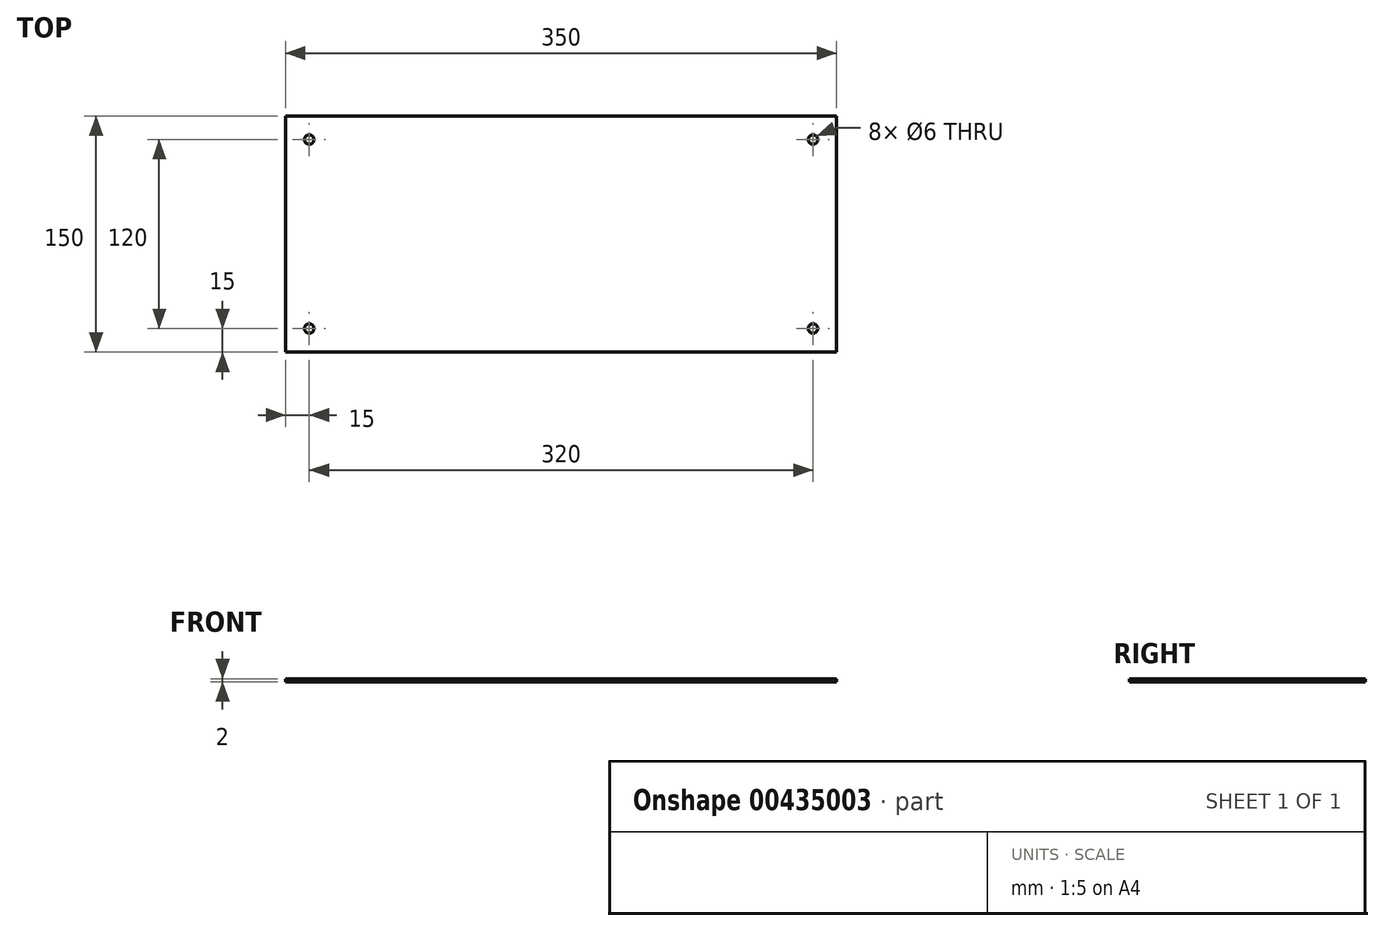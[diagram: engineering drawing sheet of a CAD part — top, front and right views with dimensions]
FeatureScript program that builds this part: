
annotation { "Feature Type Name" : "Feature", "Feature Type Description" : "" }
export const myFeature = defineFeature(function(context is Context, id is Id, definition is map)
    precondition{}
    {
        {
            var Q0;
            Q0=qCreatedBy(makeId("Top.planeOp"),FACE);
            var sketch = newSketch(context, id + "F0", { "sketchPlane" : qUnion([Q0])});
            skLineSegment(sketch, "E0.bottom", {"start": v(-175, -75) * mm, "end": v(175, -75) * mm});
            skLineSegment(sketch, "E0.top", {"start": v(-175, 75) * mm, "end": v(175, 75) * mm});
            skLineSegment(sketch, "E0.left", {"start": v(-175, -75) * mm, "end": v(-175, 75) * mm});
            skLineSegment(sketch, "E0.right", {"start": v(175, -75) * mm, "end": v(175, 75) * mm});
            skPoint(sketch, "E0.middle", {"position": v(0, 0) * mm});
            skSolve(sketch);
        }
        {
            var Q0;
            Q0 = qSketchRegion(id + "F0", true);
            extrude(context, id + "F1", {"entities" : qUnion([Q0]), "depth" : 2 * mm});
        }
        {
            var Q0;
            Q0=makeQuery(id+"F1.opExtrude","CAP_FACE",FACE,{"disambiguationData":[OSD([sQuery(id+"F0.wireOp",EDGE,"E0.bottom"),sQuery(id+"F0.wireOp",EDGE,"E0.top"),sQuery(id+"F0.wireOp",EDGE,"E0.left"),sQuery(id+"F0.wireOp",EDGE,"E0.right")])],"isStart":false});
            var sketch = newSketch(context, id + "F2", { "sketchPlane" : qUnion([Q0])});
            skLineSegment(sketch, "E1", {"start": v(-175, 75) * mm, "end": v(-175, 60) * mm});
            skLineSegment(sketch, "E2", {"start": v(-175, 60) * mm, "end": v(-160, 60) * mm});
            skLineSegment(sketch, "E3", {"start": v(-160, 60) * mm, "end": v(-160, -60) * mm});
            skLineSegment(sketch, "E4", {"start": v(-160, -60) * mm, "end": v(160, -60) * mm});
            skLineSegment(sketch, "E5", {"start": v(160, -60) * mm, "end": v(160, 60) * mm});
            skSolve(sketch);
        }
        {
            var Q0;
            Q0=sQuery(id+"F2.wireOp",VERTEX,"E3.start");
            var Q1;
            Q1=sQuery(id+"F2.wireOp",VERTEX,"E4.start");
            var Q2;
            Q2=sQuery(id+"F2.wireOp",VERTEX,"E5.end");
            var Q3;
            Q3=sQuery(id+"F2.wireOp",VERTEX,"E5.start");
            var Q4;
            Q4=makeQuery(id+"F1.opExtrude","SWEPT_BODY",BODY,{"disambiguationData":[OSD([sQuery(id+"F0.wireOp",EDGE,"E0.bottom"),sQuery(id+"F0.wireOp",EDGE,"E0.top"),sQuery(id+"F0.wireOp",EDGE,"E0.left"),sQuery(id+"F0.wireOp",EDGE,"E0.right")])]});
            hole(context, id + "F3", {"style" : HoleStyle.SIMPLE, "endStyle" : HoleEndStyle.BLIND, "holeDiameter" : 6 * mm, "holeDepth" : 150 * mm, "isTappedThrough" : true, "tappedDepth" : 12 * mm, "tapClearance" : 3, "locations" : qUnion([Q0, Q1, Q2, Q3]), "scope" : qUnion([Q4])});
        }
    });
